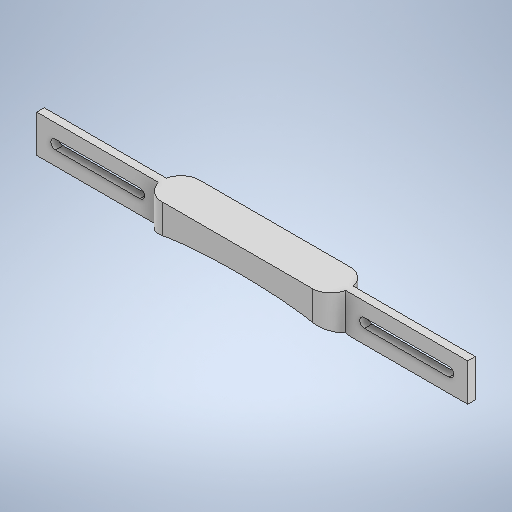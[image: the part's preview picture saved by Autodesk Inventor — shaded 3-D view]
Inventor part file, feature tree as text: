
AUTODESK INVENTOR PART (.ipt)
format: ipt  version: 2025.1 (Build 291241000, 241)  size: 317,952 bytes
history: native  units: in
note: dims shown in document units (in); Inventor stores cm internally (conversion verified against a paired STEP export)
features: sketch x3, extrude x3, fillet x2, move_body x2, direct_edit x1
ambient origin geometry x8: Origin, YZ Plane, XZ Plane, XY Plane, X Axis, Y Axis, Z Axis, Center Point
bodies: Solid1 (feature_tree)
feature tree (11):
  sketch  "Sketch1"  dims[d81=0.5in d82=0.0in d119=0.25in d135=0.25in]
  extrude  "Extrusion1"  Depth=0.25in
  fillet  "Fillet2"  Radius=0.25in
  direct_edit  "Direct Edit2"
  extrude  "Extrusion18"  Depth=0.1in TaperAngle=0.0deg
  fillet  "Fillet4"  Radius=0.8125in
  extrude  "Extrusion19"  Depth=0.125in
  sketch  "Sketch6"  dims[d136=0.1in d140=0.0in d141=0.0in d142=1.0in]
  sketch  "Sketch7"  dims[d143=0.0in d144=0.0in d145=1.0in d146=0.8125in d147=0.0in d148=0.125in d152=0.25in d153=0.0in d154=0.25in d155=180.0deg d156=0.125in d157=0.125in d158=0.8125in d159=0.0in d27=0.5in d28=0.0344in d29=0.5in d30=0.0344in]
  move_body  "Move4"
  move_body  "Move5"
